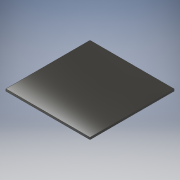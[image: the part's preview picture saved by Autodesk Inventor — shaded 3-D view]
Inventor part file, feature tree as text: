
AUTODESK INVENTOR PART (.ipt)
format: ipt  version: 2019.3 (Build 233278000, 278)  size: 94,720 bytes
history: native  units: mm
features: other x1, extrude x1, sketch x1
ambient origin geometry x8: Origin, YZ Plane, XZ Plane, XY Plane, X Axis, Y Axis, Z Axis, Center Point
bodies: Body1 (feature_tree)
feature tree (3):
  other  "ソリッド1"
  extrude  "押し出し1"  Depth=400.0mm
  sketch  "スケッチ1"
